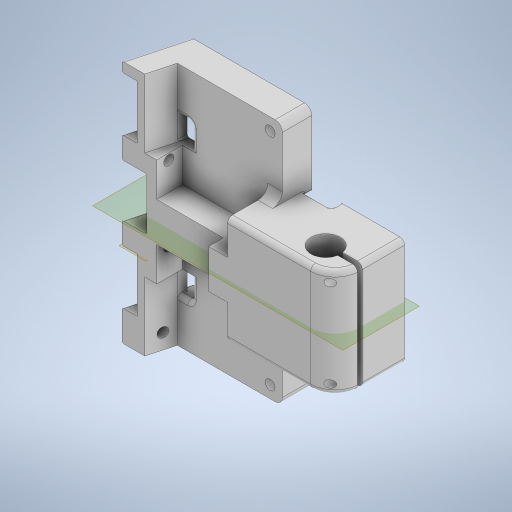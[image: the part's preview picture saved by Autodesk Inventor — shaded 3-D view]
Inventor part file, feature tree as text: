
AUTODESK INVENTOR PART (.ipt)
format: ipt  version: 2023 (Build 270158000, 158)  size: 1,102,336 bytes
history: native  units: in
note: dims shown in document units (in); Inventor stores cm internally (conversion verified against a paired STEP export)
features: projected_geometry x38, sketch x33, extrude x29, reference x26, fillet x19, other x11, hole x4, chamfer x1, mirror x1
ambient origin geometry x8: Origin, YZ Plane, XZ Plane, XY Plane, X Axis, Y Axis, Z Axis, Center Point
bodies: Body1 (feature_tree)
feature tree (162):
  other  "Bryła1"
  sketch  "Szkic1"
  other  "Płaszczyzna konstrukcyjna1"
  extrude  "Wyciągnięcie proste1"  Depth=1.9685in
  extrude  "Wyciągnięcie proste2"  Depth=1.9685in
  extrude  "Wyciągnięcie proste3"  Depth=0.8661in
  extrude  "Wyciągnięcie proste4"  Depth=0.0394in
  extrude  "Wyciągnięcie proste5"  Depth=0.0394in
  extrude  "Wyciągnięcie proste6"  Depth=0.3937in TaperAngle=0.0deg
  extrude  "Wyciągnięcie proste7"  Depth=1.9685in
  extrude  "Wyciągnięcie proste8"  Depth=0.9843in
  extrude  "Wyciągnięcie proste9"  Depth=1.9685in
  extrude  "Wyciągnięcie proste10"  Depth=0.9843in
  hole  "Otwór1"  [1 undecoded]
  hole  "Otwór2"  [1 undecoded]
  other  "Płaszczyzna konstrukcyjna2"
  extrude  "Wyciągnięcie proste12"  TaperAngle=0.0deg  [1 undecoded]
  fillet  "Zaokrąglenie1"  Radius=0.0787in
  extrude  "Wyciągnięcie proste13"  TaperAngle=0.0deg  [1 undecoded]
  extrude  "Wyciągnięcie proste14"  Depth=0.248in
  extrude  "Wyciągnięcie proste15"  Depth=0.0787in
  extrude  "Wyciągnięcie proste16"  Depth=0.2165in
  extrude  "Wyciągnięcie proste17"  Depth=0.2165in
  extrude  "Wyciągnięcie proste20"  Depth=0.4331in
  extrude  "Wyciągnięcie proste21"  Depth=0.4331in
  chamfer  "Faza1"  Distance=0.5906in
  fillet  "Zaokrąglenie7"  Radius=0.1181in
  extrude  "Wyciągnięcie proste22"  Depth=0.1181in TaperAngle=0.0deg
  extrude  "Wyciągnięcie proste23"  Depth=0.0787in TaperAngle=0.0deg
  extrude  "Wyciągnięcie proste24"  Depth=0.0197in
  extrude  "Wyciągnięcie proste25"  Depth=0.0197in
  fillet  "Zaokrąglenie11"  [1 undecoded]
  hole  "Otwór5"  [1 undecoded]
  fillet  "Zaokrąglenie13"  Radius=0.7756in
  fillet  "Zaokrąglenie14"  Radius=0.1969in
  extrude  "Wyciągnięcie proste26"  Depth=0.1772in
  fillet  "Zaokrąglenie18"  Radius=0.1772in
  extrude  "Wyciągnięcie proste27"  Depth=0.7756in TaperAngle=0.0deg
  fillet  "Zaokrąglenie20"  Radius=0.1575in
  fillet  "Zaokrąglenie22"  Radius=0.1575in
  fillet  "Zaokrąglenie23"  Radius=0.1575in
  extrude  "Wyciągnięcie proste28"  Depth=0.1575in TaperAngle=0.0deg
  extrude  "Wyciągnięcie proste29"  Depth=0.0787in
  extrude  "Wyciągnięcie proste30"  TaperAngle=0.0deg  [1 undecoded]
  fillet  "Zaokrąglenie24"  Radius=0.3937in
  fillet  "Zaokrąglenie25"  Radius=0.3937in
  other  "Płaszczyzna konstrukcyjna3"
  mirror  "Odbij1"
  extrude  "Wyciągnięcie proste31"  Depth=0.1583in
  fillet  "Zaokrąglenie26"  Radius=0.0354in
  extrude  "Wyciągnięcie proste32"  Depth=0.0354in
  hole  "Otwór6"  [1 undecoded]
  fillet  "Zaokrąglenie27"  Radius=0.0394in
  fillet  "Zaokrąglenie28"  Radius=0.0394in
  fillet  "Zaokrąglenie29"  Radius=0.0394in
  fillet  "Zaokrąglenie30"  Radius=0.1575in
  fillet  "Zaokrąglenie31"  Radius=0.3937in
  fillet  "Zaokrąglenie32"  Radius=0.1181in
  fillet  "Zaokrąglenie33"  Radius=0.1181in
  reference  "Odniesienie1"
  reference  "Odniesienie2"
  reference  "Odniesienie3"
  reference  "Odniesienie4"
  reference  "Odniesienie5"
  reference  "Odniesienie6"
  reference  "Odniesienie7"
  reference  "Odniesienie8"
  reference  "Odniesienie9"
  reference  "Odniesienie10"
  reference  "Odniesienie11"
  reference  "Odniesienie12"
  reference  "Odniesienie13"
  sketch  "Szkic2"
  reference  "Odniesienie14"
  reference  "Odniesienie15"
  reference  "Odniesienie16"
  reference  "Odniesienie17"
  reference  "Odniesienie18"
  reference  "Odniesienie19"
  reference  "Odniesienie20"
  reference  "Odniesienie21"
  reference  "Odniesienie22"
  reference  "Odniesienie23"
  sketch  "Szkic3"
  reference  "Odniesienie24"
  projected_geometry  "Pętla rzutowana1"
  sketch  "Szkic4"
  reference  "Odniesienie25"
  sketch  "Szkic5"
  projected_geometry  "Pętla rzutowana2"
  projected_geometry  "Pętla rzutowana3"
  sketch  "Szkic6"
  reference  "Odniesienie26"
  projected_geometry  "Pętla rzutowana4"
  sketch  "Szkic7"
  projected_geometry  "Pętla rzutowana5"
  sketch  "Szkic8"
  projected_geometry  "Pętla rzutowana6"
  projected_geometry  "Pętla rzutowana7"
  sketch  "Szkic9"
  projected_geometry  "Pętla rzutowana8"
  sketch  "Szkic10"
  sketch  "Szkic11"
  projected_geometry  "Pętla rzutowana9"
  sketch  "Szkic12"
  sketch  "Szkic14"
  projected_geometry  "Pętla rzutowana11"
  sketch  "Szkic15"
  projected_geometry  "Pętla rzutowana12"
  sketch  "Szkic16"
  projected_geometry  "Pętla rzutowana13"
  sketch  "Szkic18"
  projected_geometry  "Pętla rzutowana16"
  sketch  "Szkic19"
  projected_geometry  "Pętla rzutowana17"
  sketch  "Szkic20"
  projected_geometry  "Pętla rzutowana18"
  projected_geometry  "Pętla rzutowana19"
  sketch  "Szkic23"
  projected_geometry  "Pętla rzutowana21"
  sketch  "Szkic24"
  projected_geometry  "Pętla rzutowana22"
  sketch  "Szkic25"
  projected_geometry  "Pętla rzutowana23"
  projected_geometry  "Pętla rzutowana24"
  sketch  "Szkic26"
  projected_geometry  "Pętla rzutowana25"
  projected_geometry  "Pętla rzutowana26"
  sketch  "Szkic27"
  projected_geometry  "Pętla rzutowana27"
  sketch  "Szkic28"
  projected_geometry  "Pętla rzutowana28"
  sketch  "Szkic30"
  projected_geometry  "Pętla rzutowana31"
  projected_geometry  "Pętla rzutowana32"
  sketch  "Szkic31"
  projected_geometry  "Pętla rzutowana33"
  projected_geometry  "Pętla rzutowana34"
  sketch  "Szkic32"
  projected_geometry  "Pętla rzutowana35"
  sketch  "Szkic33"
  projected_geometry  "Pętla rzutowana36"
  sketch  "Szkic34"
  projected_geometry  "Pętla rzutowana37"
  sketch  "Szkic35"
  projected_geometry  "Pętla rzutowana38"
  sketch  "Szkic36"
  projected_geometry  "Pętla rzutowana39"
  projected_geometry  "Pętla rzutowana40"
  sketch  "Szkic37"
  projected_geometry  "Pętla rzutowana41"
  sketch  "Szkic38"
  projected_geometry  "Pętla rzutowana42"
  projected_geometry  "Pętla rzutowana43"
  projected_geometry  "Pętla rzutowana44"
  other  "<userpath>\Documents\PROJECTS - repos\Stratos---MicroSumo\mechanics\byk_alternator.iam"
  other  "byk_alternator.iam"
  other  "servo_mini_1370hd_cos:1"
  other  "servo_mini_1370hd_cos:2"
  other  "Zespół1"
  other  "uchwyt silnikow:1"
  other  "noz2:1"
note: 8 required parameter values undecoded (feature->parameter linkage not recoverable at this tier; creation-order binding heuristic only, values carry confidence <= 0.55)
